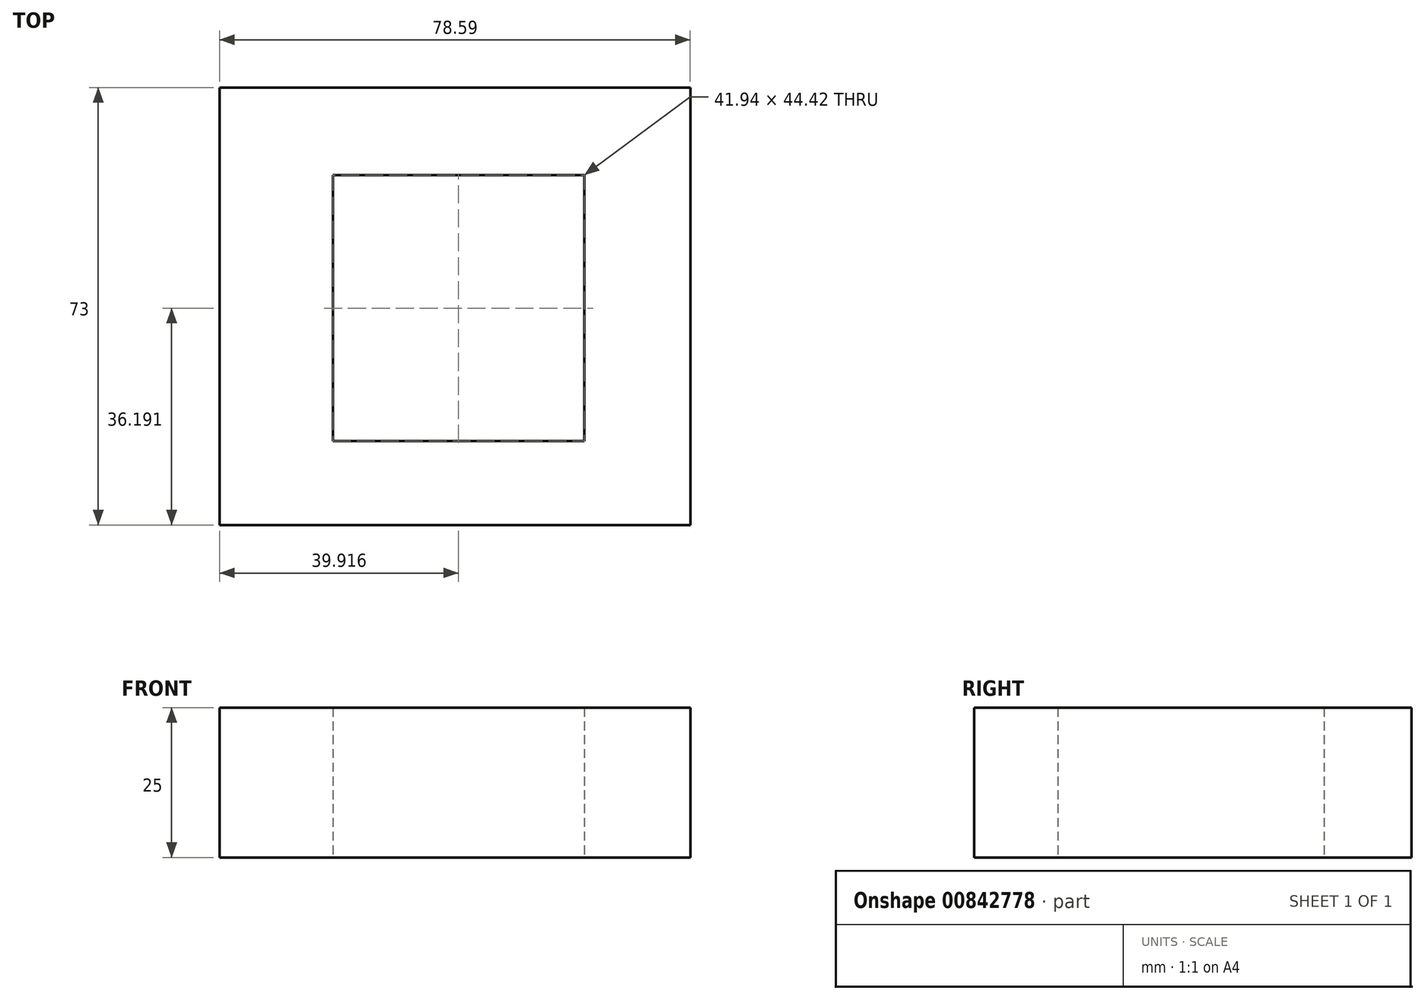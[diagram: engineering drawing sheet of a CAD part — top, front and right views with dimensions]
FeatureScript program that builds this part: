
annotation { "Feature Type Name" : "Feature", "Feature Type Description" : "" }
export const myFeature = defineFeature(function(context is Context, id is Id, definition is map)
    precondition{}
    {
        {
            var Q0;
            Q0=qCreatedBy(makeId("Top.planeOp"),FACE);
            var sketch = newSketch(context, id + "F0", { "sketchPlane" : qUnion([Q0])});
            skLineSegment(sketch, "E0", {"start": v(-38.99, 35.1) * mm, "end": v(36.81, 35.1) * mm});
            skLineSegment(sketch, "E1", {"start": v(36.81, 35.1) * mm, "end": v(36.81, -37.9) * mm});
            skLineSegment(sketch, "E2", {"start": v(36.81, -37.9) * mm, "end": v(-41.78, -37.9) * mm});
            skLineSegment(sketch, "E3", {"start": v(-41.78, -37.9) * mm, "end": v(-41.78, 35.1) * mm});
            skLineSegment(sketch, "E4", {"start": v(-41.78, 35.1) * mm, "end": v(-38.99, 35.1) * mm});
            skLineSegment(sketch, "E5", {"start": v(36.81, -37.9) * mm, "end": v(19.1, -23.92) * mm});
            skLineSegment(sketch, "E6", {"start": v(19.1, -23.92) * mm, "end": v(-22.83, -23.92) * mm});
            skLineSegment(sketch, "E7", {"start": v(-22.83, -23.92) * mm, "end": v(-41.78, -37.9) * mm});
            skLineSegment(sketch, "E8", {"start": v(-22.83, -23.92) * mm, "end": v(-22.83, 20.5) * mm});
            skLineSegment(sketch, "E9", {"start": v(-22.83, 20.5) * mm, "end": v(-41.78, 35.1) * mm});
            skLineSegment(sketch, "E10", {"start": v(-22.83, 20.5) * mm, "end": v(19.1, 20.5) * mm});
            skLineSegment(sketch, "E11", {"start": v(19.1, 20.5) * mm, "end": v(36.81, 35.1) * mm});
            skLineSegment(sketch, "E12", {"start": v(19.1, -23.92) * mm, "end": v(19.1, 20.5) * mm});
            skCircle(sketch, "E13", {"center": v(0, 0) * mm, "radius": 6.94 * mm});
            skSolve(sketch);
        }
        {
            var Q0;
            Q0 = qSketchRegion(id + "F0", true);
            extrude(context, id + "F1", {"entities" : qUnion([Q0]), "depth" : 25 * mm, "offsetDistance" : 25 * mm});
        }
    });
